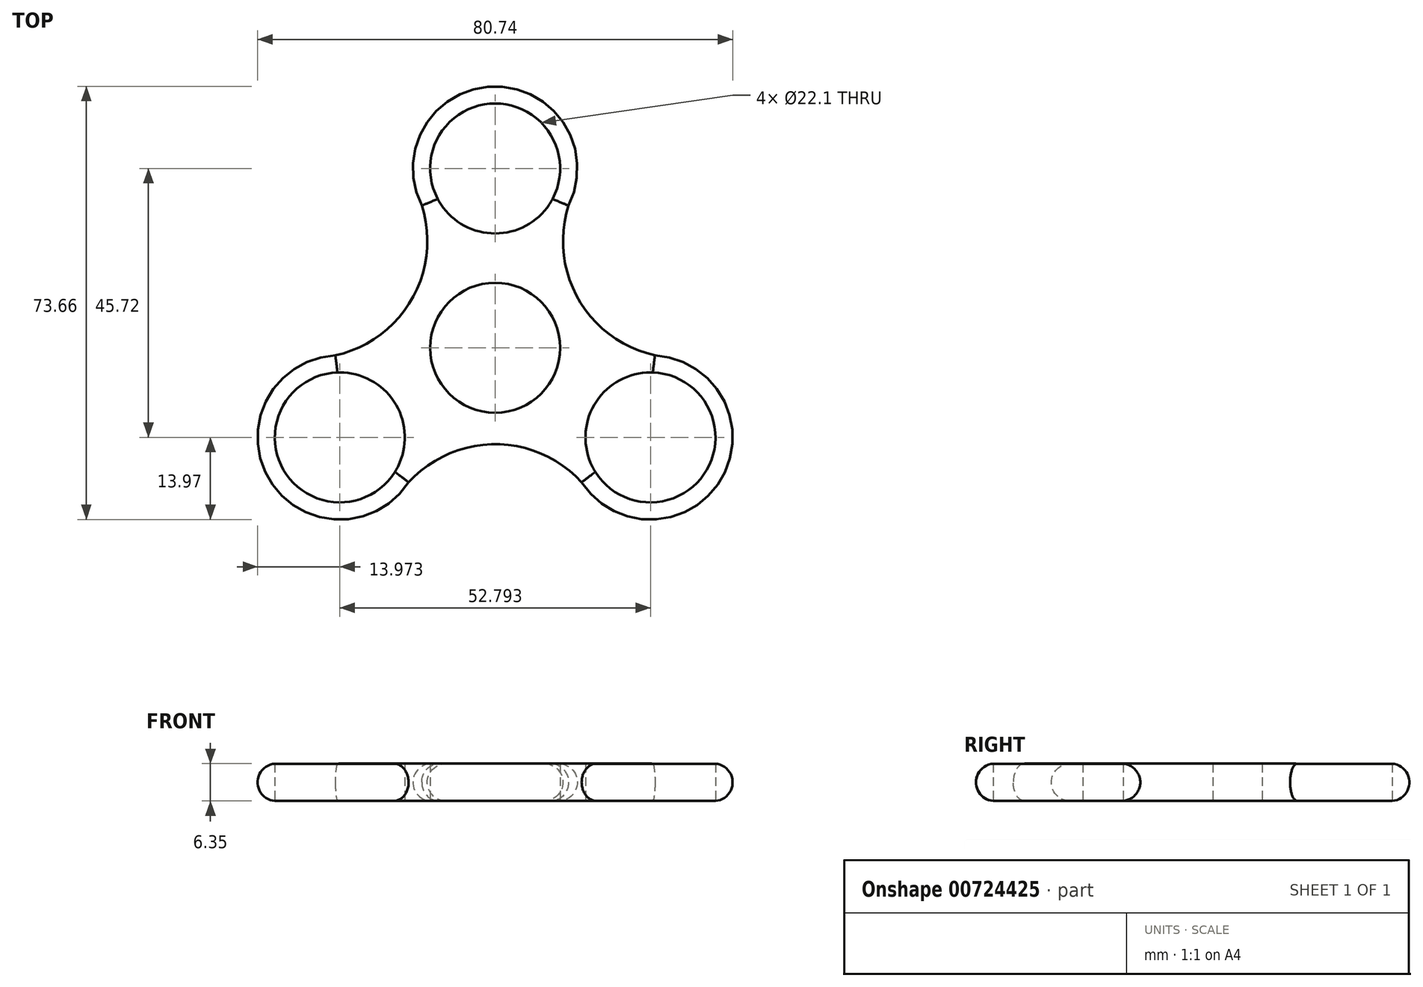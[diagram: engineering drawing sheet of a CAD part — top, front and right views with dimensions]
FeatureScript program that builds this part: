
annotation { "Feature Type Name" : "Feature", "Feature Type Description" : "" }
export const myFeature = defineFeature(function(context is Context, id is Id, definition is map)
    precondition{}
    {
        {
            var Q0;
            Q0=qCreatedBy(makeId("Top.planeOp"),FACE);
            var sketch = newSketch(context, id + "F0", { "sketchPlane" : qUnion([Q0])});
            skCircle(sketch, "E0", {"center": v(0, 0) * mm, "radius": 11.05 * mm});
            skLineSegment(sketch, "E1", {"start": v(0, 1.42) * mm, "end": v(0, 30.48) * mm});
            skCircle(sketch, "E2", {"center": v(0, 30.48) * mm, "radius": 11.05 * mm});
            skCircle(sketch, "E3", {"center": v(0, 30.48) * mm, "radius": 13.97 * mm});
            skCircle(sketch, "E4.1.0", {"center": v(-26.4, -15.24) * mm, "radius": 13.97 * mm});
            skCircle(sketch, "E4.1.1", {"center": v(-26.4, -15.24) * mm, "radius": 11.05 * mm});
            skCircle(sketch, "E4.2.0", {"center": v(26.4, -15.24) * mm, "radius": 13.97 * mm});
            skCircle(sketch, "E4.2.1", {"center": v(26.4, -15.24) * mm, "radius": 11.05 * mm});
            skLineSegment(sketch, "E5", {"start": v(-1.23, 0.7) * mm, "end": v(-14.2, 8.2) * mm});
            skArc(sketch, "E6.filletArc", {"start": v(-1.23, 0.7) * mm, "mid": v(-0.4, 0.7) * mm, "end": v(0, 1.42) * mm});
            skPoint(sketch, "E7.center.orphan", {"position": v(-35.08, 20.26) * mm});
            skPoint(sketch, "E8.orphan", {"position": v(-30.01, -1.4) * mm});
            skArc(sketch, "E9", {"start": v(-29.77, -1.68) * mm, "mid": v(-14.2, 8.2) * mm, "end": v(-13.43, 26.63) * mm});
            skArc(sketch, "E10.1.0", {"start": v(16.35, -24.94) * mm, "mid": v(0, -16.4) * mm, "end": v(-16.35, -24.94) * mm});
            skArc(sketch, "E10.2.0", {"start": v(13.43, 26.63) * mm, "mid": v(14.2, 8.2) * mm, "end": v(29.77, -1.68) * mm});
            skPoint(sketch, "E11.orphan", {"position": v(-68.94, 39.8) * mm});
            skSolve(sketch);
        }
        {
            var Q0;
            Q0 = qSketchRegion(id + "F0", true);
            extrude(context, id + "F1", {"entities" : qUnion([Q0]), "depth" : 6.35 * mm, "offsetDistance" : 25.4 * mm});
        }
        {
            var Q0;
            Q0=makeQuery(id+"F1.opExtrude","CAP_EDGE",EDGE,{"disambiguationData":[OSD([sQuery(id+"F0.wireOp",EDGE,"E4.2.0")])],"isStart":true});
            var Q1;
            Q1=makeQuery(id+"F1.opExtrude","CAP_EDGE",EDGE,{"disambiguationData":[OSD([sQuery(id+"F0.wireOp",EDGE,"E10.2.0")])],"isStart":true});
            var Q2;
            Q2=makeQuery(id+"F1.opExtrude","CAP_EDGE",EDGE,{"disambiguationData":[OSD([sQuery(id+"F0.wireOp",EDGE,"E3")])],"isStart":true});
            var Q3;
            Q3=makeQuery(id+"F1.opExtrude","CAP_EDGE",EDGE,{"disambiguationData":[OSD([sQuery(id+"F0.wireOp",EDGE,"E9")])],"isStart":true});
            var Q4;
            Q4=makeQuery(id+"F1.opExtrude","CAP_EDGE",EDGE,{"disambiguationData":[OSD([sQuery(id+"F0.wireOp",EDGE,"E4.1.0")])],"isStart":true});
            var Q5;
            Q5=makeQuery(id+"F1.opExtrude","CAP_EDGE",EDGE,{"disambiguationData":[OSD([sQuery(id+"F0.wireOp",EDGE,"E10.1.0")])],"isStart":true});
            fillet(context, id + "F2", {"entities" : qUnion([Q0, Q1, Q2, Q3, Q4, Q5]), "radius" : 3.17 * mm, "tangentPropagation" : true, "allowEdgeOverflow" : false});
        }
        {
            var Q0;
            Q0=makeQuery(id+"F1.opExtrude","CAP_EDGE",EDGE,{"disambiguationData":[OSD([sQuery(id+"F0.wireOp",EDGE,"E9")])],"isStart":false});
            var Q1;
            Q1=makeQuery(id+"F1.opExtrude","CAP_EDGE",EDGE,{"disambiguationData":[OSD([sQuery(id+"F0.wireOp",EDGE,"E4.1.0")])],"isStart":false});
            var Q2;
            Q2=makeQuery(id+"F1.opExtrude","CAP_EDGE",EDGE,{"disambiguationData":[OSD([sQuery(id+"F0.wireOp",EDGE,"E10.1.0")])],"isStart":false});
            var Q3;
            Q3=makeQuery(id+"F1.opExtrude","CAP_EDGE",EDGE,{"disambiguationData":[OSD([sQuery(id+"F0.wireOp",EDGE,"E4.2.0")])],"isStart":false});
            var Q4;
            Q4=makeQuery(id+"F1.opExtrude","CAP_EDGE",EDGE,{"disambiguationData":[OSD([sQuery(id+"F0.wireOp",EDGE,"E10.2.0")])],"isStart":false});
            var Q5;
            Q5=makeQuery(id+"F1.opExtrude","CAP_EDGE",EDGE,{"disambiguationData":[OSD([sQuery(id+"F0.wireOp",EDGE,"E3")])],"isStart":false});
            fillet(context, id + "F3", {"entities" : qUnion([Q0, Q1, Q2, Q3, Q4, Q5]), "radius" : 3.17 * mm, "tangentPropagation" : true, "allowEdgeOverflow" : false});
        }
    });
